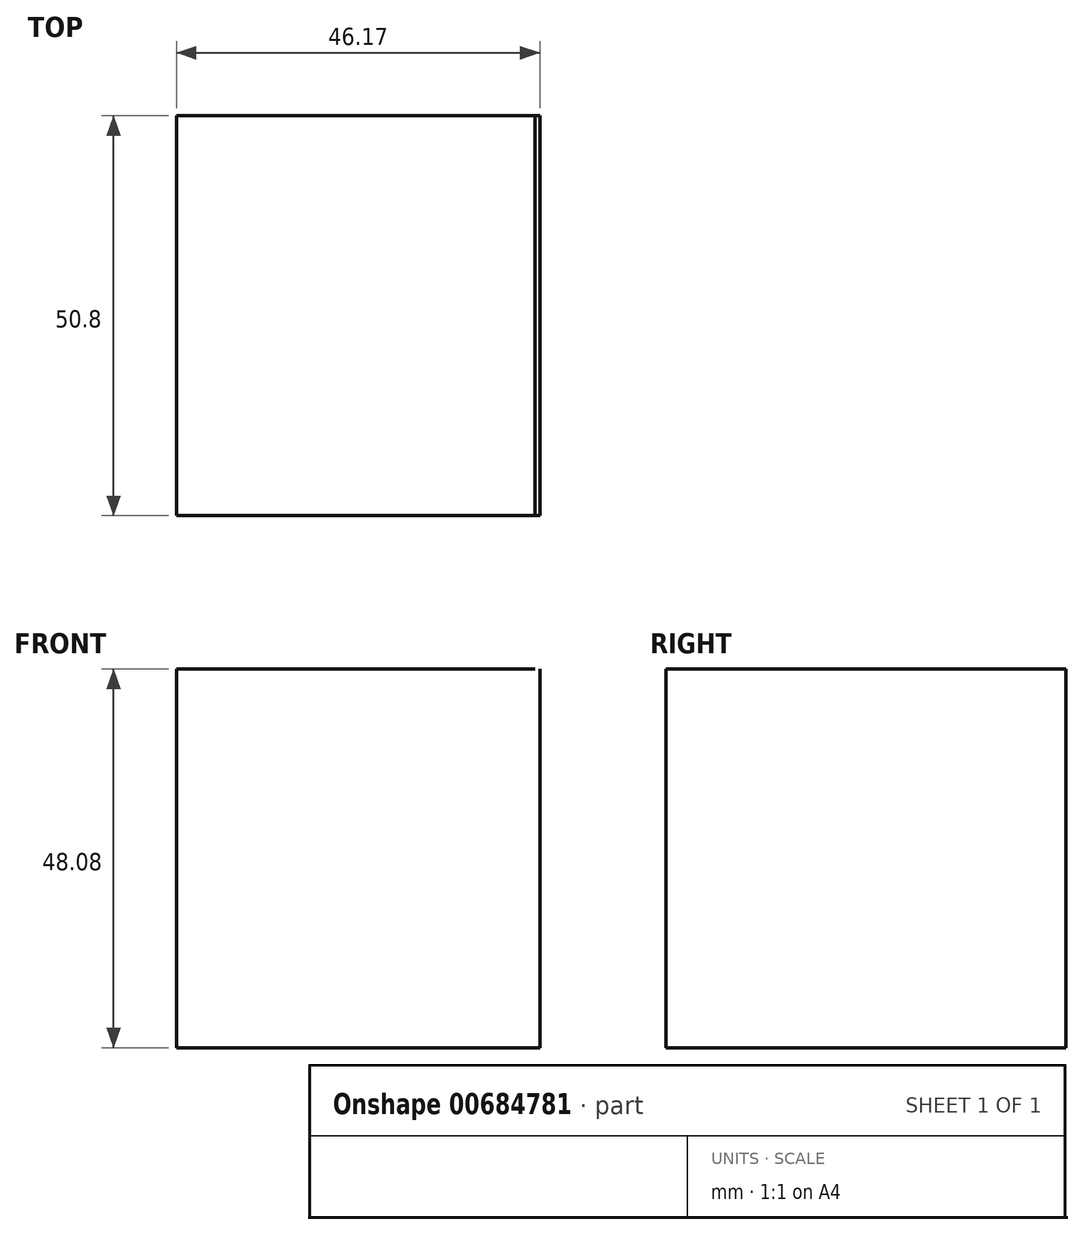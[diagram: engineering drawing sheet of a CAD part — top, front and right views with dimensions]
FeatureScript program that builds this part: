
annotation { "Feature Type Name" : "Feature", "Feature Type Description" : "" }
export const myFeature = defineFeature(function(context is Context, id is Id, definition is map)
    precondition{}
    {
        {
            var Q0;
            Q0=qCreatedBy(makeId("Front.planeOp"),FACE);
            var sketch = newSketch(context, id + "F0", { "sketchPlane" : qUnion([Q0])});
            skLineSegment(sketch, "E0", {"start": v(-46.17, 0) * mm, "end": v(0, 0) * mm});
            skLineSegment(sketch, "E1", {"start": v(0, 0) * mm, "end": v(0, 48.08) * mm});
            skLineSegment(sketch, "E2", {"start": v(-0.64, 48.08) * mm, "end": v(-46.17, 48.08) * mm});
            skLineSegment(sketch, "E3", {"start": v(-46.17, 48.08) * mm, "end": v(-46.17, 0) * mm});
            skSolve(sketch);
        }
        {
            var Q0;
            Q0=sQuery(id+"F0.wireOp",EDGE,"E2");
            var Q1;
            Q1=sQuery(id+"F0.wireOp",EDGE,"E1");
            var Q2;
            Q2=sQuery(id+"F0.wireOp",EDGE,"E0");
            var Q3;
            Q3=sQuery(id+"F0.wireOp",EDGE,"E3");
            extrude(context, id + "F1", {"bodyType" : ToolBodyType.SURFACE, "operationType" : NewBodyOperationType.ADD, "surfaceEntities" : qUnion([Q0, Q1, Q2, Q3]), "depth" : 25.4 * mm, "offsetDistance" : 25.4 * mm, "hasSecondDirection" : true, "secondDirectionOppositeDirection" : true, "secondDirectionDepth" : 25.4 * mm});
        }
    });
